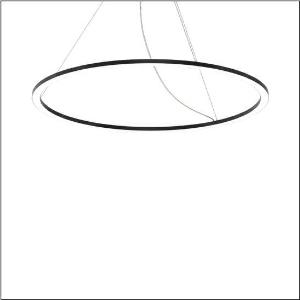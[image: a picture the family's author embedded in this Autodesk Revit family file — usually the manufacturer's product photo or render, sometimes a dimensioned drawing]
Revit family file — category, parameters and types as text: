
# Revit family: silica_21_ring-d_5pjbd4d3104a
name_source: partatom
category: Lighting Fixtures
units: mm (PartAtom-declared; Revit-internal decimal feet)

## family parameters
Cut with Voids When Loaded = No
Host = Face
Light Source = No
Part Type = Normal
Room Calculation Point = No
Round Connector Dimension = Use Diameter
Shared = No

## types (1)
- Silica 21 Ring-D (1 x LED, 11350 lm, 125 W, 4000K)
    Apparent Load = 125 VA
    CIE Flux Codes = 37 69 92 100 100
    Color Rendering = 80
    Color Temperature = 4000K
    Default Elevation = 1800 mm
    Description = Silica 21 Ring-D, suspended luminaire, of PMMA, frosted, light emission: ring underside luminous distribution, primary light characteristic: symmetric, installation type: suspended mounting, LED, rated luminous flux: 11.350lm, luminous efficacy: 91lm/W, light colour: 840, colour temperature: 4000K, control gear: DALI 2, with terminal, 5-pole, mains connection: 230V, AC/DC, 0/50..60Hz, rated input power: 125W, housing, of extruded aluminium section, jet black (RAL 9005), diameter: 1.450mm, ceiling canopy, jet black (RAL 9005), protection rating (lamp compartment): IP40, protection rating (control gear compartment): IP40, insulation class (complete): insulation class I (protective earthing), certification: CE, impact resistance: IK02, permissible operating ambient temperature: 0..+35°C, packaging unit: 1 piece
    Height = 25 mm  [stored 0.082021 ft]
    Lamp = 1 x LED
    Lamp Light Flux = 11350 lm
    Lamp Power = 125 W
    Lamp count = 1
    Length = 1450 mm
    Luminous efficacy = 91 lm/W
    Manufacturer = Siteco
    ModVariant = No
    Model = 5PJBD4D3104A
    Mounting Place = Ceiling
    Mounting Type = Pendant
    Number of Poles = 1
    OnlyDefault = Yes
    Power Factor = 1
    Product Name = Silica 21 Ring-D
    Product group = suspended luminaire
    ProductGroupID = 904
    Protection Class = Protection class I
    Protection Degree = IP 40
    RLX_Detail_Level = 1
    RLX_Emergency_Light_Flux = 0 lm
    RLX_Emergency_Type = 0
    RLX_Emergency_Type_DB = No
    RlxData = <blob elided: 19397 chars, md5=3cc432e9>
    Socket = socket
    Standby Power = 0 W
    System Light Flux = 11350 lm
    System Power = 125 W
    Type Comments = Product without accessories
    Type Image = l_1258357.jpg
    URL = http://relux.com
    VarID = ---
    Voltage = 0 V
    Weight = 0.00 kg
    Width = 0 mm  [stored 0 ft]

note: [stored X ft] marks values corroborated as IEEE doubles in the binary element streams (Revit-internal decimal feet)

## geometry (parser evidence)
native form markers: Blend x4, Sweep x10
no freeform markers — native parametric forms only
